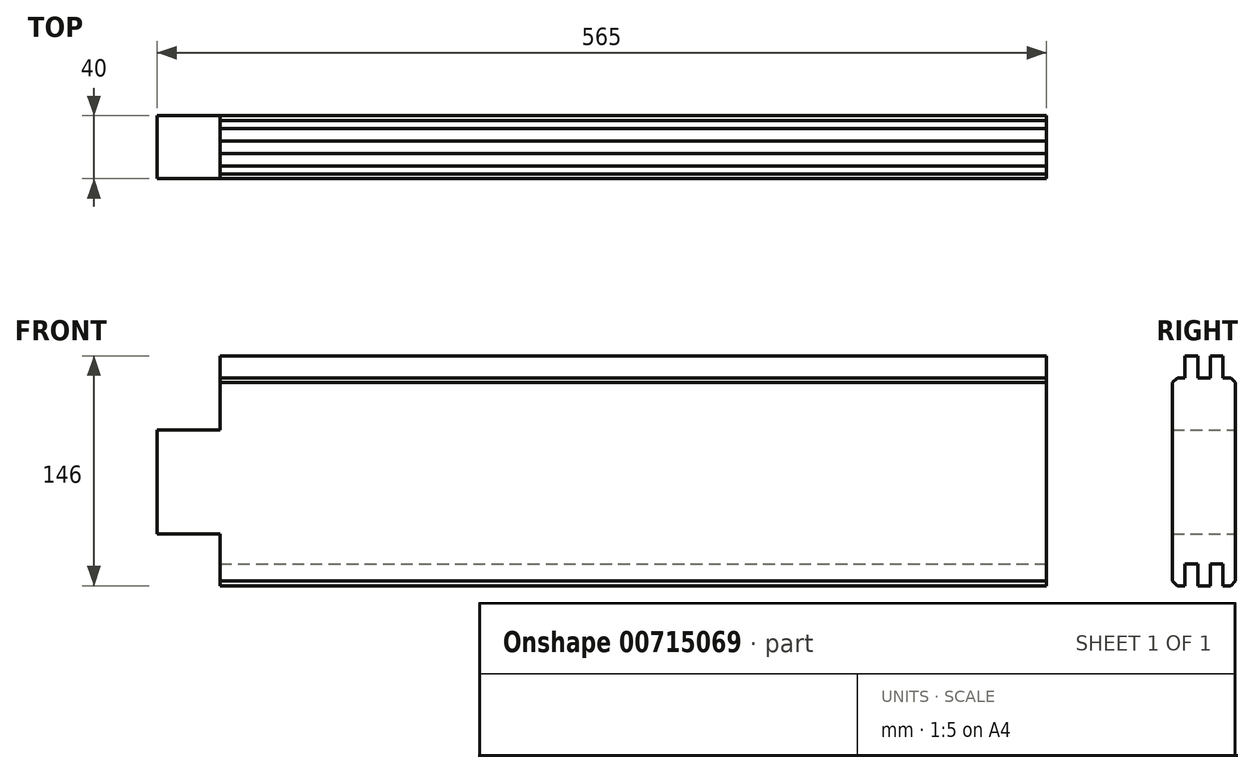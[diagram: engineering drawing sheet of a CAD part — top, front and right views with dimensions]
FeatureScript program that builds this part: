
annotation { "Feature Type Name" : "Feature", "Feature Type Description" : "" }
export const myFeature = defineFeature(function(context is Context, id is Id, definition is map)
    precondition{}
    {
        {
            var Q0;
            Q0=qCreatedBy(makeId("Right.planeOp"),FACE);
            var sketch = newSketch(context, id + "F0", { "sketchPlane" : qUnion([Q0])});
            skLineSegment(sketch, "E0", {"start": v(20, 63) * mm, "end": v(20, -63) * mm});
            skLineSegment(sketch, "E1", {"start": v(20, -63) * mm, "end": v(17, -66) * mm});
            skLineSegment(sketch, "E2", {"start": v(17, -66) * mm, "end": v(12, -66) * mm});
            skLineSegment(sketch, "E3", {"start": v(12, -52) * mm, "end": v(12, -66) * mm});
            skLineSegment(sketch, "E4", {"start": v(12, -52) * mm, "end": v(4, -52) * mm});
            skLineSegment(sketch, "E5", {"start": v(4, -66) * mm, "end": v(4, -52) * mm});
            skLineSegment(sketch, "E6", {"start": v(4, -66) * mm, "end": v(-4, -66) * mm});
            skLineSegment(sketch, "E7", {"start": v(-4, -52) * mm, "end": v(-4, -66) * mm});
            skLineSegment(sketch, "E8", {"start": v(-4, -52) * mm, "end": v(-12, -52) * mm});
            skLineSegment(sketch, "E9", {"start": v(-12, -66) * mm, "end": v(-12, -52) * mm});
            skLineSegment(sketch, "E10", {"start": v(-12, -66) * mm, "end": v(-17, -66) * mm});
            skLineSegment(sketch, "E11", {"start": v(-17, -66) * mm, "end": v(-20, -63) * mm});
            skLineSegment(sketch, "E12", {"start": v(-20, -63) * mm, "end": v(-20, 63) * mm});
            skLineSegment(sketch, "E13", {"start": v(-20, 63) * mm, "end": v(-17, 66) * mm});
            skLineSegment(sketch, "E14", {"start": v(-17, 66) * mm, "end": v(-12, 66) * mm});
            skLineSegment(sketch, "E15", {"start": v(-4, 66) * mm, "end": v(4, 66) * mm});
            skLineSegment(sketch, "E16", {"start": v(12, 66) * mm, "end": v(17, 66) * mm});
            skLineSegment(sketch, "E17", {"start": v(17, 66) * mm, "end": v(20, 63) * mm});
            skPoint(sketch, "E18.end.orphan", {"position": v(12, 57.8) * mm});
            skPoint(sketch, "E19.end.orphan", {"position": v(4, 66.3) * mm});
            skPoint(sketch, "E20.end.orphan", {"position": v(-4, 66.3) * mm});
            skLineSegment(sketch, "E21", {"start": v(-12, 66) * mm, "end": v(-12, 80) * mm});
            skLineSegment(sketch, "E22", {"start": v(-12, 80) * mm, "end": v(-4, 80) * mm});
            skLineSegment(sketch, "E23", {"start": v(-4, 80) * mm, "end": v(-4, 66) * mm});
            skLineSegment(sketch, "E24", {"start": v(4, 66) * mm, "end": v(4, 80) * mm});
            skLineSegment(sketch, "E25", {"start": v(4, 80) * mm, "end": v(12, 80) * mm});
            skLineSegment(sketch, "E26", {"start": v(12, 80) * mm, "end": v(12, 66) * mm});
            skLineSegment(sketch, "E27", {"start": v(20, -33) * mm, "end": v(-20, -33) * mm});
            skLineSegment(sketch, "E28", {"start": v(20, 33) * mm, "end": v(-20, 33) * mm});
            skPoint(sketch, "E29.end.orphan", {"position": v(-141.42, 0) * mm});
            skLineSegment(sketch, "E30", {"start": v(20, 0) * mm, "end": v(-20, 0) * mm});
            skLineSegment(sketch, "E31", {"start": v(20, 0) * mm, "end": v(-20, 0) * mm, "construction": true});
            skLineSegment(sketch, "E32", {"start": v(0, 33) * mm, "end": v(0, -33) * mm, "construction": true});
            skSolve(sketch);
        }
        {
            var Q0;
            Q0=qCreatedBy(makeId("Front.planeOp"),FACE);
            var sketch = newSketch(context, id + "F1", { "sketchPlane" : qUnion([Q0])});
            skLineSegment(sketch, "E33", {"start": v(565, 0) * mm, "end": v(-565, 0) * mm, "construction": true});
            skPoint(sketch, "E34.right.start.orphan", {"position": v(-259.12, 108.1) * mm});
            skPoint(sketch, "E35.left.start.orphan", {"position": v(237.35, 108.1) * mm});
            skPoint(sketch, "E36.left.end.orphan", {"position": v(237.35, -84.05) * mm});
            skPoint(sketch, "E36.bottom.start.orphan", {"position": v(237.35, -117.05) * mm});
            skPoint(sketch, "E37.right.start.orphan", {"position": v(-259.12, -117.05) * mm});
            skPoint(sketch, "E37.top.end.orphan", {"position": v(-259.12, -84.05) * mm});
            skLineSegment(sketch, "E38.bottom", {"start": v(-605, 33) * mm, "end": v(-525, 33) * mm});
            skLineSegment(sketch, "E38.top", {"start": v(-605, 133) * mm, "end": v(-525, 133) * mm});
            skLineSegment(sketch, "E38.left", {"start": v(-605, 33) * mm, "end": v(-605, 133) * mm});
            skLineSegment(sketch, "E38.right", {"start": v(-525, 33) * mm, "end": v(-525, 133) * mm});
            skPoint(sketch, "E38.middle", {"position": v(-565, 83) * mm});
            skLineSegment(sketch, "E39.bottom", {"start": v(-605, -133) * mm, "end": v(-525, -133) * mm});
            skLineSegment(sketch, "E39.top", {"start": v(-605, -33) * mm, "end": v(-525, -33) * mm});
            skLineSegment(sketch, "E39.left", {"start": v(-605, -133) * mm, "end": v(-605, -33) * mm});
            skLineSegment(sketch, "E39.right", {"start": v(-525, -133) * mm, "end": v(-525, -33) * mm});
            skPoint(sketch, "E39.middle", {"position": v(-565, -83) * mm});
            skLineSegment(sketch, "E40.bottom", {"start": v(605, 33) * mm, "end": v(525, 33) * mm});
            skLineSegment(sketch, "E40.top", {"start": v(605, 133) * mm, "end": v(525, 133) * mm});
            skLineSegment(sketch, "E40.left", {"start": v(605, 33) * mm, "end": v(605, 133) * mm});
            skLineSegment(sketch, "E40.right", {"start": v(525, 33) * mm, "end": v(525, 133) * mm});
            skPoint(sketch, "E40.middle", {"position": v(565, 83) * mm});
            skLineSegment(sketch, "E41.bottom", {"start": v(605, -33) * mm, "end": v(525, -33) * mm});
            skLineSegment(sketch, "E41.top", {"start": v(605, -133) * mm, "end": v(525, -133) * mm});
            skLineSegment(sketch, "E41.left", {"start": v(605, -33) * mm, "end": v(605, -133) * mm});
            skLineSegment(sketch, "E41.right", {"start": v(525, -33) * mm, "end": v(525, -133) * mm});
            skPoint(sketch, "E41.middle", {"position": v(565, -83) * mm});
            skSolve(sketch);
        }
        {
            var Q0;
            {var subQ0=sQuery(id+"F0.wireOp",EDGE,"E28");Q0=makeQuery(id+"F0.imprint","IMPRINT",FACE,{"disambiguationData":[TD([[makeQuery(id+"F0.imprint","IMPRINT",EDGE,{"derivedFrom":subQ0}),1.0]])]});}
            var Q1;
            {var subQ3=sQuery(id+"F0.wireOp",EDGE,"E13");Q1=makeQuery(id+"F0.imprint","IMPRINT",FACE,{"disambiguationData":[TD([[makeQuery(id+"F0.imprint","IMPRINT",EDGE,{"derivedFrom":subQ3}),-1.0]])]});}
            var Q2;
            {var subQ0=sQuery(id+"F0.wireOp",EDGE,"E27");Q2=makeQuery(id+"F0.imprint","IMPRINT",FACE,{"disambiguationData":[TD([[makeQuery(id+"F0.imprint","IMPRINT",EDGE,{"derivedFrom":subQ0}),-1.0]])]});}
            var Q3;
            {var subQ1=sQuery(id+"F0.wireOp",EDGE,"E1");Q3=makeQuery(id+"F0.imprint","IMPRINT",FACE,{"disambiguationData":[TD([[makeQuery(id+"F0.imprint","IMPRINT",EDGE,{"derivedFrom":subQ1}),-1.0]])]});}
            extrude(context, id + "F2", {"entities" : qUnion([Q0, Q1, Q2, Q3]), "oppositeDirection" : true, "depth" : 565 * mm, "offsetDistance" : 25 * mm});
        }
        {
            var Q0;
            Q0=makeQuery(id+"F1.imprint","IMPRINT",FACE,{"disambiguationData":[TD([[makeQuery(id+"F1.imprint","IMPRINT",EDGE,{"derivedFrom":sQuery(id+"F1.wireOp",EDGE,"E38.bottom")}),1.0]])]});
            var Q1;
            Q1=makeQuery(id+"F1.imprint","IMPRINT",FACE,{"disambiguationData":[TD([[makeQuery(id+"F1.imprint","IMPRINT",EDGE,{"derivedFrom":sQuery(id+"F1.wireOp",EDGE,"E39.bottom")}),1.0]])]});
            extrude(context, id + "F3", {"entities" : qUnion([Q0, Q1]), "operationType" : NewBodyOperationType.REMOVE, "endBound" : BoundingType.SYMMETRIC, "oppositeDirection" : true, "depth" : 50 * mm, "offsetDistance" : 25 * mm});
        }
    });
